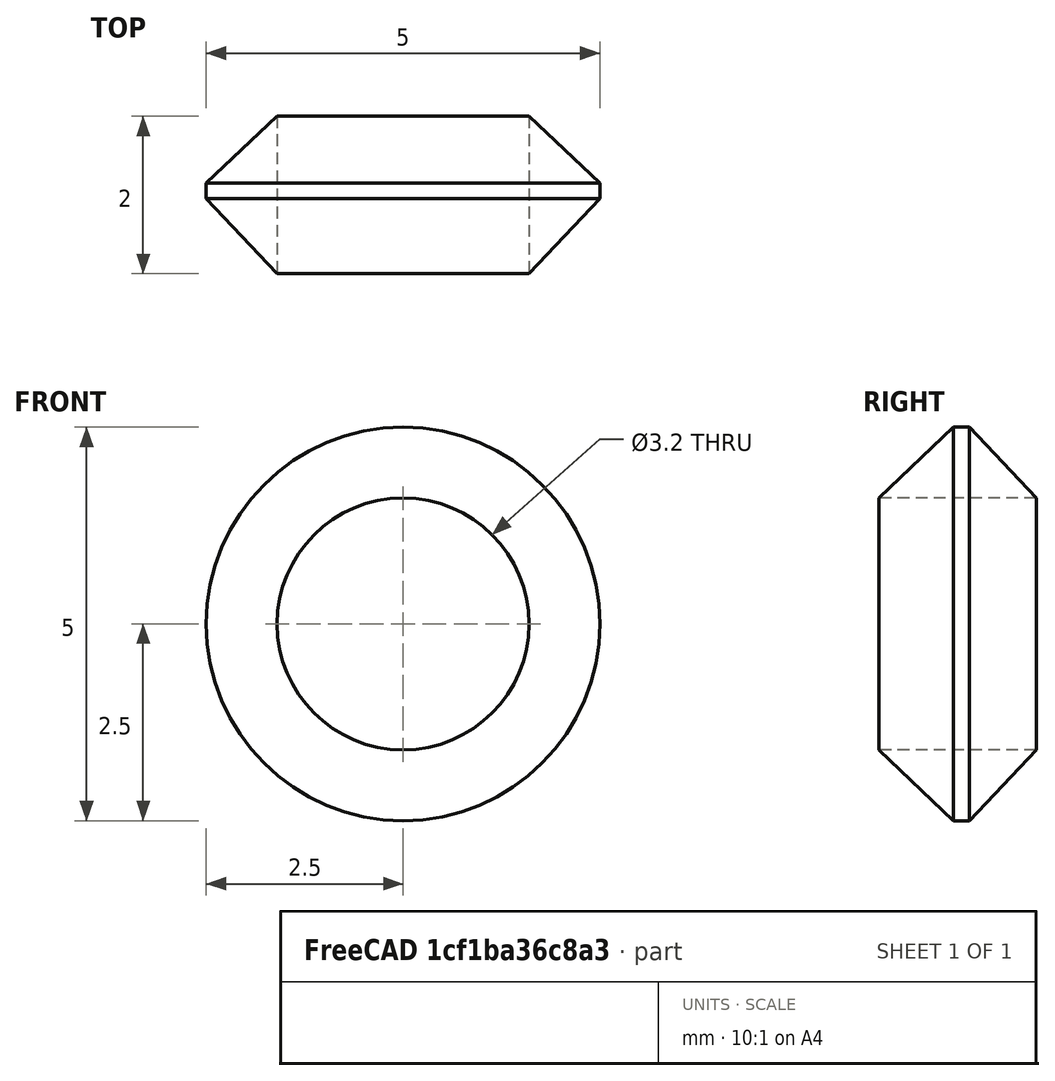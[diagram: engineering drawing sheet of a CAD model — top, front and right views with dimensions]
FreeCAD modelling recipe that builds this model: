
FCSTD DOCUMENT  (FreeCAD 0.19R20209 (Git))
Label: Afstandstykke_2mm
License: Creative Commons Attribution
LicenseURL: http://creativecommons.org/licenses/by/4.0/
objects: Sketcher::SketchObject×1, PartDesign::Revolution×1, PartDesign::Body×1
note: 4 computed .brp shape members not serialized (recipe doc carries the construction recipe); baked Part::Feature solids carry a one-line shape summary decoded from their .brp

FEATURE [Sketcher::SketchObject] Sketch
  MapMode = 5
  Support = -> [XY_Plane]
  expr: Constraints[5] = 3.2 / 2
  expr: Constraints[6] = 5 / 2
  sketch-geometry (4):
    g0: LineSegment StartX=-1.6 StartY=1 StartZ=0 EndX=-1.6 EndY=-1 EndZ=0
    g1: LineSegment StartX=-1.6 StartY=-1 StartZ=0 EndX=-2.5 EndY=-0.0482153 EndZ=0
    g2: LineSegment StartX=-2.5 StartY=-0.0482153 StartZ=0 EndX=-2.5 EndY=0.148967 EndZ=0
    g3: LineSegment StartX=-2.5 StartY=0.148967 StartZ=0 EndX=-1.6 EndY=1 EndZ=0
  constraints (10):
    c: Coincident(g0,g1)
    c: Coincident(g1,g2)
    c: Vertical(g2)
    c: Coincident(g2,g3)
    c: Coincident(g3,g0)
    c: DistanceX(g0,g-1) = 1.6
    c: DistanceX(g1,g-1) = 2.5
    c: Symmetric(g0,g0,g-1)
    c: DistanceY(g0,g0) = 2
    c: Angle(g1,g3) = 1.5708
FEATURE [PartDesign::Revolution] Revolution
  Angle = 360
  Axis = (0,1,0)
  Base = (0,0,0)
  Profile = -> Sketch
  ReferenceAxis = -> Sketch [V_Axis]
  Refine = true
FEATURE [PartDesign::Body] Body
  Group = -> [Sketch,Revolution]
  Origin = -> Origin
  Tip = -> Revolution
